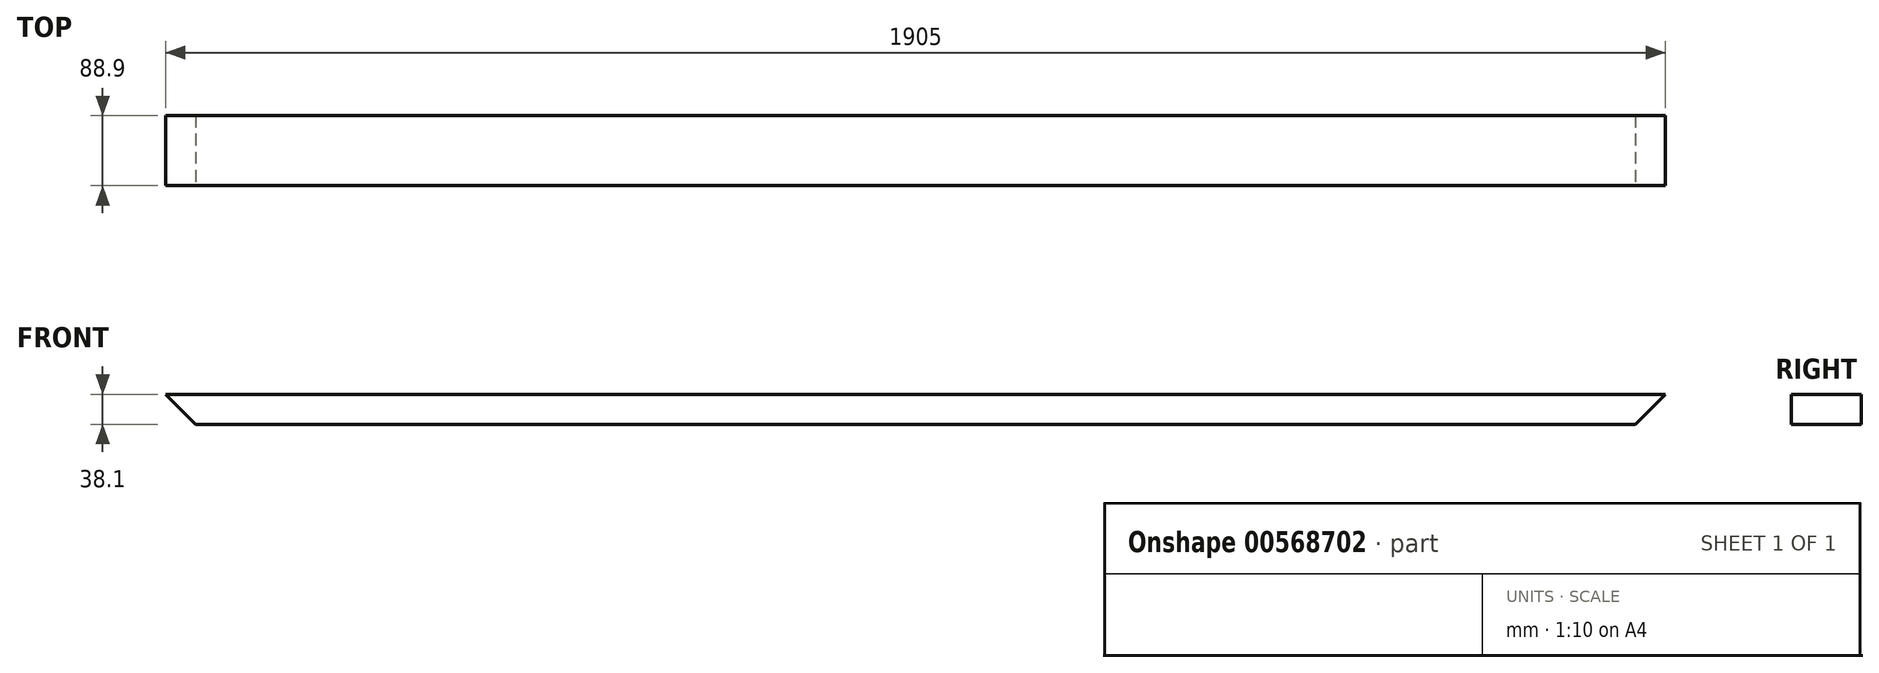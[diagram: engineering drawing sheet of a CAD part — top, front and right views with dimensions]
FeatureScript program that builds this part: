
annotation { "Feature Type Name" : "Feature", "Feature Type Description" : "" }
export const myFeature = defineFeature(function(context is Context, id is Id, definition is map)
    precondition{}
    {
        {
            var Q0;
            Q0=qCreatedBy(makeId("Front.planeOp"),FACE);
            var sketch = newSketch(context, id + "F0", { "sketchPlane" : qUnion([Q0])});
            skLineSegment(sketch, "E0.bottom", {"start": v(-952.5, -19.05) * mm, "end": v(952.5, -19.05) * mm});
            skLineSegment(sketch, "E0.top", {"start": v(-952.5, 19.05) * mm, "end": v(952.5, 19.05) * mm});
            skLineSegment(sketch, "E0.left", {"start": v(-952.5, -19.05) * mm, "end": v(-952.5, 19.05) * mm});
            skLineSegment(sketch, "E0.right", {"start": v(952.5, -19.05) * mm, "end": v(952.5, 19.05) * mm});
            skPoint(sketch, "E0.middle", {"position": v(0, 0) * mm});
            skSolve(sketch);
        }
        {
            var Q0;
            Q0 = qSketchRegion(id + "F0", true);
            extrude(context, id + "F1", {"entities" : qUnion([Q0]), "depth" : 88.9 * mm, "offsetDistance" : 25.4 * mm});
        }
        {
            var Q0;
            Q0=makeQuery(id+"F1.opExtrude","CAP_FACE",FACE,{"disambiguationData":[OSD([sQuery(id+"F0.wireOp",EDGE,"E0.bottom"),sQuery(id+"F0.wireOp",EDGE,"E0.top"),sQuery(id+"F0.wireOp",EDGE,"E0.left"),sQuery(id+"F0.wireOp",EDGE,"E0.right")])],"isStart":false});
            var sketch = newSketch(context, id + "F2", { "sketchPlane" : qUnion([Q0])});
            skLineSegment(sketch, "E1", {"start": v(-952.5, 19.05) * mm, "end": v(-952.5, -19.05) * mm});
            skLineSegment(sketch, "E2", {"start": v(-952.5, -19.05) * mm, "end": v(-914.4, -19.05) * mm});
            skLineSegment(sketch, "E3", {"start": v(-914.4, -19.05) * mm, "end": v(-952.5, 19.05) * mm});
            skLineSegment(sketch, "E4", {"start": v(952.5, 19.05) * mm, "end": v(914.4, -19.05) * mm});
            skLineSegment(sketch, "E5", {"start": v(914.4, -19.05) * mm, "end": v(952.5, -19.05) * mm});
            skLineSegment(sketch, "E6", {"start": v(952.5, -19.05) * mm, "end": v(952.5, 19.05) * mm});
            skSolve(sketch);
        }
        {
            var Q0;
            Q0 = qSketchRegion(id + "F2", true);
            extrude(context, id + "F3", {"entities" : qUnion([Q0]), "operationType" : NewBodyOperationType.REMOVE, "endBound" : BoundingType.THROUGH_ALL, "oppositeDirection" : true, "depth" : 25.4 * mm, "offsetDistance" : 25.4 * mm});
        }
    });
